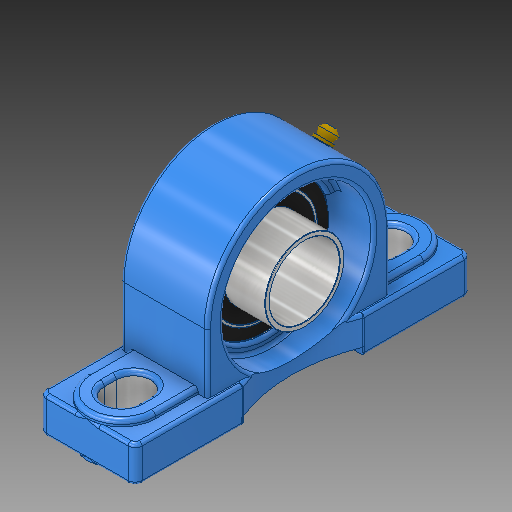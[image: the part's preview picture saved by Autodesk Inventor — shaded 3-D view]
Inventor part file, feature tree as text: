
AUTODESK INVENTOR PART (.ipt)
format: ipt  version: 2019 (Build 230136000, 136)  size: 804,352 bytes
history: native  units: mm
features: sketch x28, extrude x23, fillet x14, plane x8, mirror x6, revolve x1
ambient origin geometry x8: Origin, YZ Plane, XZ Plane, XY Plane, X Axis, Y Axis, Z Axis, Center Point
bodies: Solid1 (feature_tree)
feature tree (80):
  extrude  "Extrusion1"  Depth=167.0mm
  fillet  "Fillet1"  Radius=23.8mm
  plane  "Work Plane1"
  extrude  "Extrusion2"  Depth=18.0mm TaperAngle=0.0deg
  sketch  "Sketch3"  dims[d6=3.5mm d10=43.0mm d11=0.0mm]
  extrude  "Extrusion3"  Depth=43.0mm TaperAngle=0.0deg
  sketch  "Sketch4"  dims[d14=3.0mm d15=0.0mm d18=3.0mm d19=0.0mm]
  extrude  "Extrusion4"  Depth=3.0mm TaperAngle=0.0deg
  plane  "Work Plane2"
  mirror  "Mirror1"
  extrude  "Extrusion5"  Depth=74.25mm
  sketch  "Sketch7"  dims[d29=65.0mm d30=18.0mm d31=0.0mm]
  extrude  "Extrusion6"  Depth=18.0mm TaperAngle=0.0deg
  extrude  "Extrusion7"  Depth=18.0mm TaperAngle=0.0deg
  extrude  "Extrusion8"  Depth=1.58mm
  extrude  "Extrusion9"  Depth=1.58mm
  plane  "Work Plane4"
  mirror  "Mirror3"
  fillet  "Fillet2"  Radius=1.58mm
  fillet  "Fillet3"  Radius=1.58mm
  fillet  "Fillet4"  Radius=1.58mm
  fillet  "Fillet5"  [1 undecoded]
  plane  "Work Plane5"
  mirror  "Mirror4"
  fillet  "Fillet6"  Radius=65.0mm
  fillet  "Fillet7"  Radius=54.0mm
  plane  "Work Plane6"
  revolve  "Revolution1"  [1 undecoded]
  sketch  "Sketch14"  dims[d73=12.8mm d74=0.0mm d75=12.8mm d76=0.0mm]
  sketch  "Sketch15"  dims[d77=0.2mm d78=0.2mm]
  plane  "Work Plane7"
  extrude  "Extrusion10"  Depth=52.0mm
  plane  "Work Plane8"
  extrude  "Extrusion11"  Depth=12.8mm TaperAngle=0.0deg
  extrude  "Extrusion12"  Depth=0.2mm
  extrude  "Extrusion13"  Depth=42.9mm TaperAngle=0.0deg
  fillet  "Fillet8"  Radius=0.2mm
  fillet  "Fillet9"  Radius=0.2mm
  fillet  "Fillet10"  Radius=4.0mm
  extrude  "Extrusion14"  Depth=18.0mm TaperAngle=0.0deg
  fillet  "Fillet11"  Radius=63.5mm
  fillet  "Fillet12"  Radius=3.0mm
  extrude  "Extrusion15"  Depth=18.0mm TaperAngle=0.0deg
  sketch  "Sketch23"  dims[d105=3.0mm d106=17.0mm]
  sketch  "Sketch24"  dims[d107=21.0mm d108=0.0mm d109=2.0mm]
  extrude  "Extrusion16"  Depth=3.0mm TaperAngle=0.0deg
  sketch  "Sketch25"
  extrude  "Extrusion17"  Depth=2.0mm TaperAngle=0.0deg
  sketch  "Sketch26"
  extrude  "Extrusion18"  Depth=18.0mm
  extrude  "Extrusion19"  Depth=17.0mm
  extrude  "Extrusion20"  Depth=2.0mm
  fillet  "Fillet13"  [1 undecoded]
  plane  "Work Plane9"
  extrude  "Extrusion21"  [1 undecoded]
  extrude  "Extrusion22"  [1 undecoded]
  mirror  "Mirror5"
  mirror  "Mirror6"
  mirror  "Mirror7"
  extrude  "Extrusion23"  [1 undecoded]
  fillet  "Fillet14"  [1 undecoded]
  sketch  "Sketch1"  dims[d0=47.6mm d1=167.0mm d2=23.8mm]
  sketch  "Sketch2"  dims[d3=83.5mm d4=18.0mm d5=0.0mm]
  sketch  "Sketch5"  dims[d20=17.78mm d21=0.0mm d22=74.25mm]
  sketch  "Sketch6"  dims[d23=12.7mm d24=0.0mm d27=18.0mm d28=0.0mm]
  sketch  "Sketch8"  dims[d34=8.0mm d35=0.0mm d36=1.58mm]
  sketch  "Sketch9"  dims[d37=1.58mm d38=1.58mm d39=1.58mm d40=1.58mm d41=1.58mm d56=90.0deg]
  sketch  "Sketch10"  dims[d62=24.5mm d63=18.4mm d64=0.0mm d65=0.0mm d66=65.0mm d67=54.0mm]
  sketch  "Sketch11"  dims[d68=52.0mm d69=13.0mm d70=0.0mm]
  sketch  "Sketch13"  dims[d71=54.0mm d72=52.0mm]
  sketch  "Sketch17"  dims[d79=0.2mm d80=42.9mm d81=0.0mm d82=0.2mm d83=0.2mm d84=4.0mm d85=0.0mm]
  sketch  "Sketch18"  dims[d86=100.0mm d87=0.0mm d88=18.0mm d89=0.0mm d90=63.5mm d91=3.0mm]
  sketch  "Sketch19"  dims[d92=17.0mm d93=18.0mm d94=0.0mm]
  sketch  "Sketch20"  dims[d95=3.0mm d96=0.0mm d97=565.0mm d98=0.0mm]
  sketch  "Sketch21"  dims[d99=2.0mm d100=565.0mm d101=0.0mm]
  sketch  "Sketch22"  dims[d102=18.0mm d103=0.0mm d104=63.5mm]
  sketch  "Sketch27"
  sketch  "Sketch28"
  sketch  "Sketch29"
  sketch  "Sketch30"
note: 7 required parameter values undecoded (feature->parameter linkage not recoverable at this tier; creation-order binding heuristic only, values carry confidence <= 0.55)